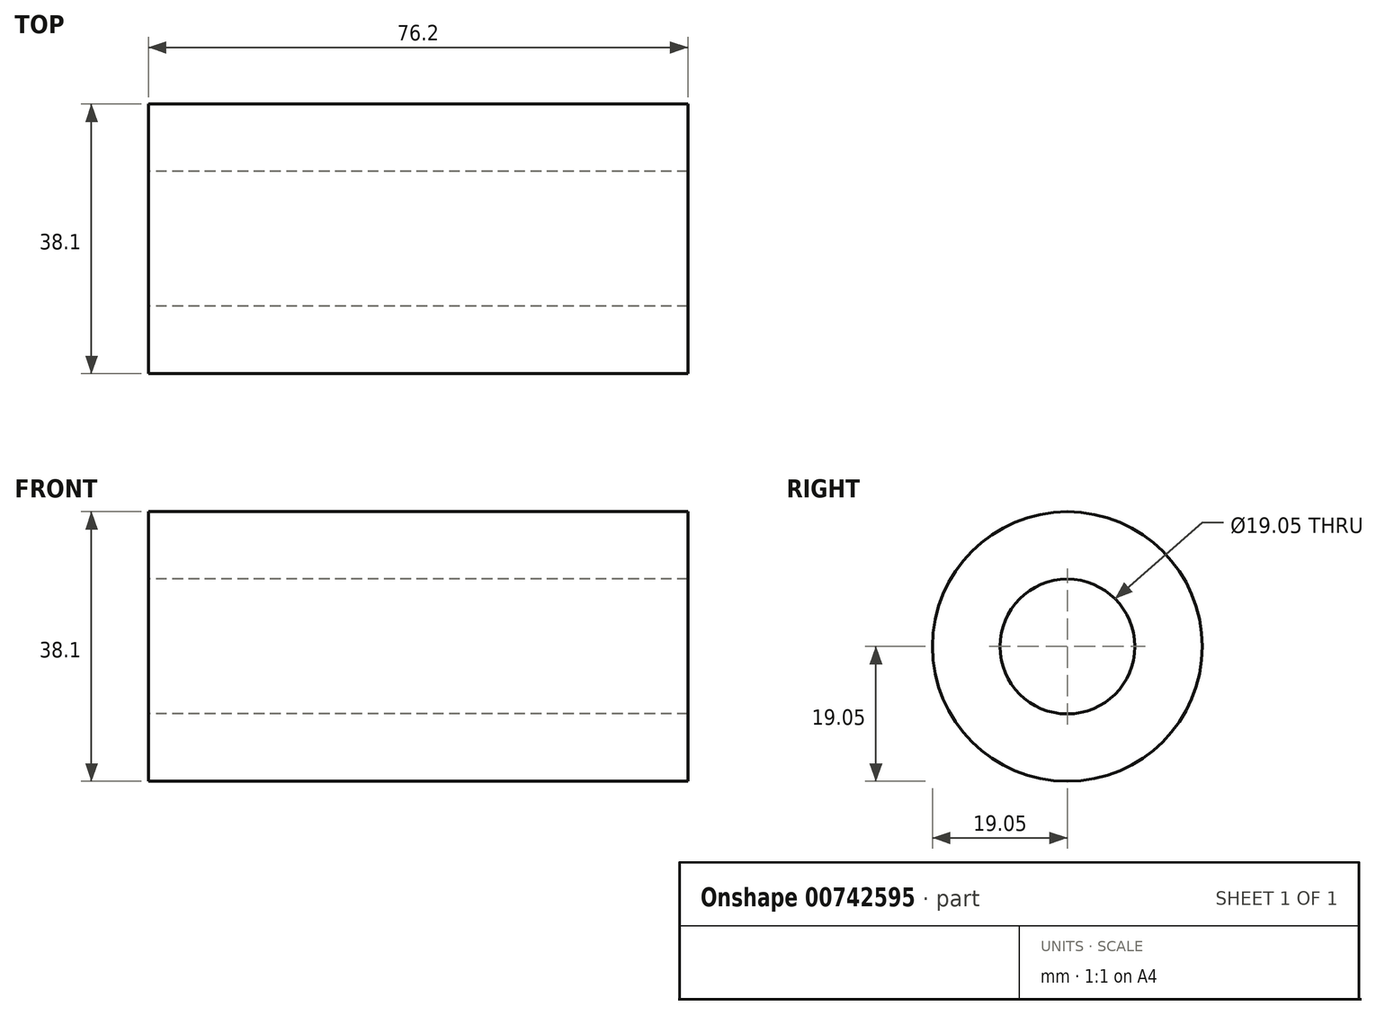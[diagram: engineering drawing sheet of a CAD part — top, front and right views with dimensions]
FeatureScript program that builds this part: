
annotation { "Feature Type Name" : "Feature", "Feature Type Description" : "" }
export const myFeature = defineFeature(function(context is Context, id is Id, definition is map)
    precondition{}
    {
        {
            var Q0;
            Q0=qCreatedBy(makeId("Right.planeOp"),FACE);
            var sketch = newSketch(context, id + "F0", { "sketchPlane" : qUnion([Q0])});
            skCircle(sketch, "E0", {"center": v(0, 0) * mm, "radius": 19.05 * mm});
            skCircle(sketch, "E1", {"center": v(0, 0) * mm, "radius": 9.53 * mm});
            skSolve(sketch);
        }
        {
            var Q0;
            Q0 = qSketchRegion(id + "F0", true);
            extrude(context, id + "F1", {"entities" : qUnion([Q0]), "depth" : 76.2 * mm, "offsetDistance" : 25.4 * mm});
        }
    });
